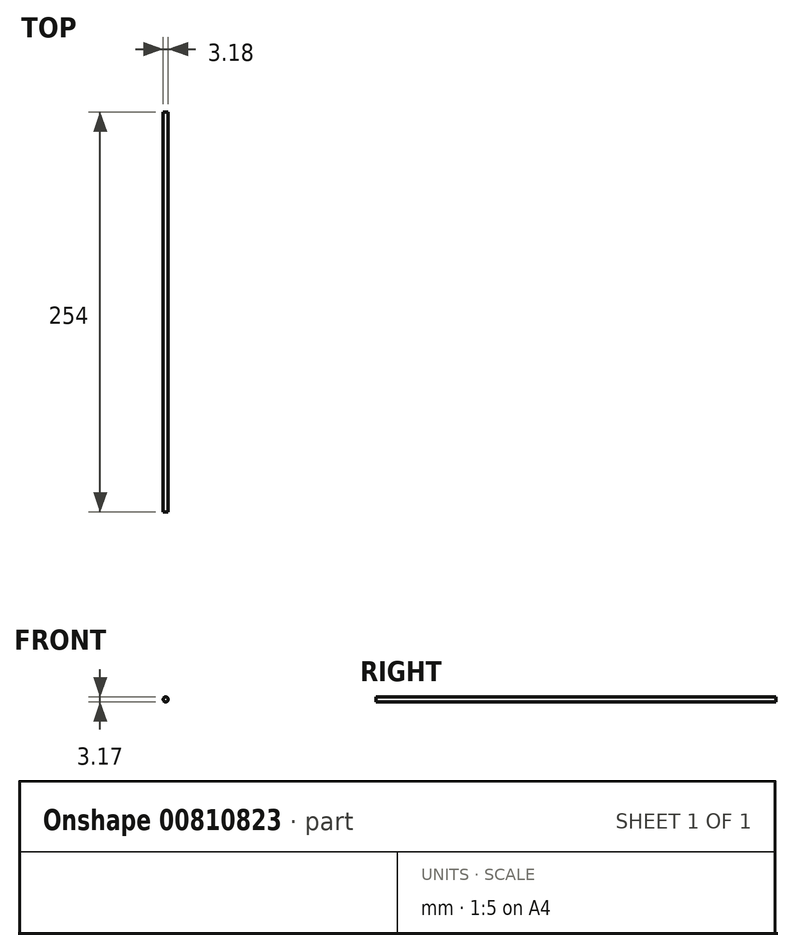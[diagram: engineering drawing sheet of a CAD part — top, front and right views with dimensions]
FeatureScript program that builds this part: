
annotation { "Feature Type Name" : "Feature", "Feature Type Description" : "" }
export const myFeature = defineFeature(function(context is Context, id is Id, definition is map)
    precondition{}
    {
        {
            var Q0;
            Q0=qCreatedBy(makeId("Front.planeOp"),FACE);
            var sketch = newSketch(context, id + "F0", { "sketchPlane" : qUnion([Q0])});
            skCircle(sketch, "E0", {"center": v(-11.15, 17.26) * mm, "radius": 1.59 * mm});
            skSolve(sketch);
        }
        {
            var Q0;
            Q0 = qSketchRegion(id + "F0", true);
            extrude(context, id + "F1", {"entities" : qUnion([Q0]), "depth" : 254 * mm, "offsetDistance" : 25.4 * mm});
        }
    });
